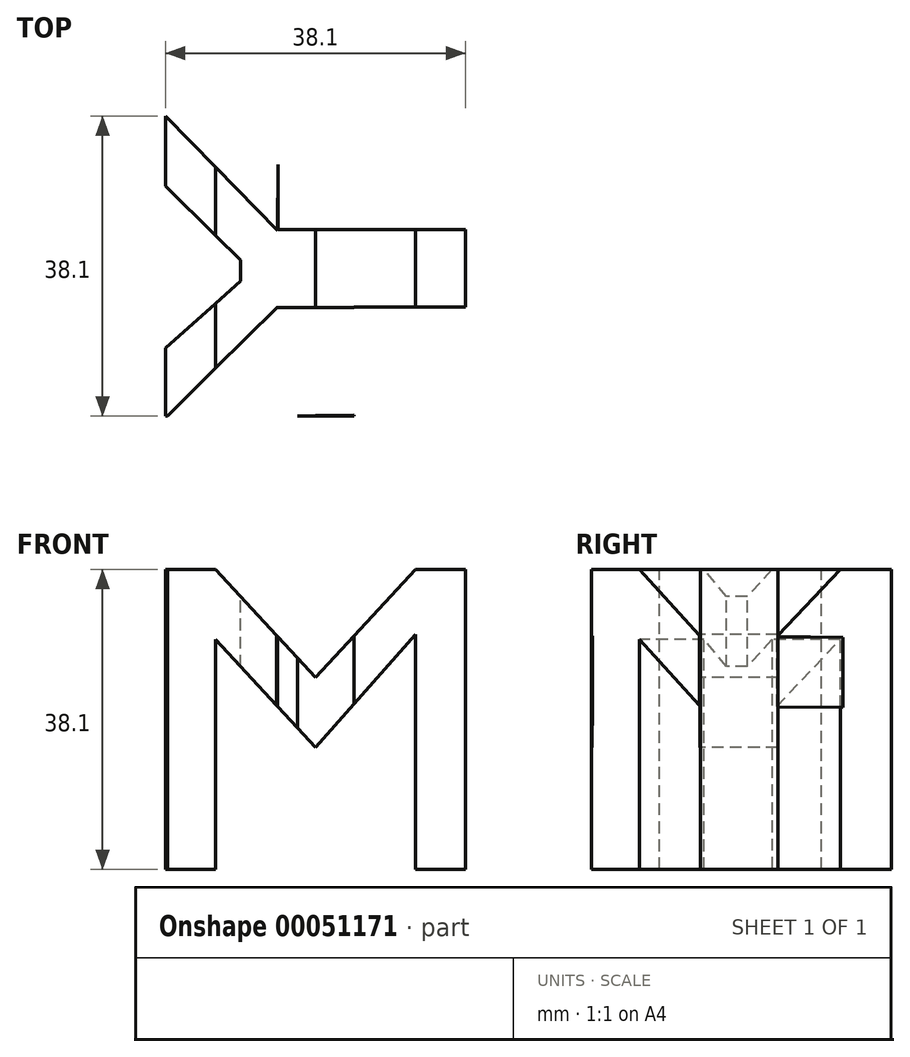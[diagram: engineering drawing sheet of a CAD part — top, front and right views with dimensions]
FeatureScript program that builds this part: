
annotation { "Feature Type Name" : "Feature", "Feature Type Description" : "" }
export const myFeature = defineFeature(function(context is Context, id is Id, definition is map)
    precondition{}
    {
        {
            var Q0;
            Q0=qCreatedBy(makeId("Front.planeOp"),FACE);
            var sketch = newSketch(context, id + "F0", { "sketchPlane" : qUnion([Q0])});
            skLineSegment(sketch, "E0.bottom", {"start": v(0, 0) * mm, "end": v(38.1, 0) * mm});
            skLineSegment(sketch, "E0.top", {"start": v(0, 38.1) * mm, "end": v(38.1, 38.1) * mm});
            skLineSegment(sketch, "E0.left", {"start": v(0, 0) * mm, "end": v(0, 38.1) * mm});
            skLineSegment(sketch, "E0.right", {"start": v(38.1, 0) * mm, "end": v(38.1, 38.1) * mm});
            skSolve(sketch);
        }
        {
            var Q0;
            Q0 = qSketchRegion(id + "F0", true);
            extrude(context, id + "F1", {"entities" : qUnion([Q0]), "depth" : 38.1 * mm});
        }
        {
            var Q0;
            Q0=makeQuery(id+"F1.opExtrude","CAP_FACE",FACE,{"disambiguationData":[OSD([sQuery(id+"F0.wireOp",EDGE,"E0.bottom"),sQuery(id+"F0.wireOp",EDGE,"E0.top"),sQuery(id+"F0.wireOp",EDGE,"E0.left"),sQuery(id+"F0.wireOp",EDGE,"E0.right")])],"isStart":false});
            var sketch = newSketch(context, id + "F2", { "sketchPlane" : qUnion([Q0])});
            skLineSegment(sketch, "E1", {"start": v(0, 38.1) * mm, "end": v(6.35, 38.1) * mm});
            skLineSegment(sketch, "E2", {"start": v(31.75, 38.1) * mm, "end": v(38.1, 38.1) * mm});
            skLineSegment(sketch, "E3", {"start": v(6.35, 38.1) * mm, "end": v(19.02, 24.39) * mm});
            skLineSegment(sketch, "E4", {"start": v(19.02, 24.39) * mm, "end": v(31.75, 38.1) * mm});
            skLineSegment(sketch, "E5", {"start": v(6.35, 29.21) * mm, "end": v(19.02, 15.5) * mm});
            skLineSegment(sketch, "E6", {"start": v(19.02, 15.5) * mm, "end": v(31.75, 29.87) * mm});
            skLineSegment(sketch, "E7", {"start": v(6.35, 29.21) * mm, "end": v(6.35, 0) * mm});
            skLineSegment(sketch, "E8", {"start": v(6.35, 29.21) * mm, "end": v(6.35, 38.1) * mm});
            skLineSegment(sketch, "E9", {"start": v(31.75, 38.1) * mm, "end": v(31.75, 0) * mm});
            skLineSegment(sketch, "E10", {"start": v(6.35, 0) * mm, "end": v(31.75, 0) * mm});
            skLineSegment(sketch, "E11", {"start": v(31.75, 29.87) * mm, "end": v(31.75, 0) * mm});
            skSolve(sketch);
        }
        {
            var Q0;
            {var subQ0=sQuery(id+"F2.wireOp",EDGE,"E3");Q0=makeQuery(id+"F2.imprint","IMPRINT",FACE,{"disambiguationData":[TD([[makeQuery(id+"F2.imprint","IMPRINT",EDGE,{"derivedFrom":subQ0}),1.0]])]});}
            extrude(context, id + "F3", {"entities" : qUnion([Q0]), "operationType" : NewBodyOperationType.REMOVE, "oppositeDirection" : true, "depth" : 38.1 * mm});
        }
        {
            var Q0;
            Q0=makeQuery(id+"F2.imprint","IMPRINT",FACE,{"disambiguationData":[TD([[makeQuery(id+"F2.imprint","IMPRINT",EDGE,{"derivedFrom":sQuery(id+"F2.wireOp",EDGE,"E5")}),-1.0]])]});
            extrude(context, id + "F4", {"entities" : qUnion([Q0]), "operationType" : NewBodyOperationType.REMOVE, "oppositeDirection" : true, "depth" : 38.1 * mm});
        }
        {
            var Q0;
            Q0=qCreatedBy(makeId("Top.planeOp"),FACE);
            cPlane(context, id + "F5", {"entities" : qUnion([Q0]), "cplaneType" : CPlaneType.OFFSET, "offset" : 38.1 * mm, "width" : 152.4 * mm, "height" : 152.4 * mm});
        }
        {
            var Q0;
            Q0=qCreatedBy(id+"F5.planeOp",FACE);
            var sketch = newSketch(context, id + "F6", { "sketchPlane" : qUnion([Q0])});
            skLineSegment(sketch, "E12", {"start": v(0, -38.33) * mm, "end": v(14.2, -24.26) * mm});
            skLineSegment(sketch, "E13", {"start": v(0, 0) * mm, "end": v(14.2, -14.53) * mm});
            skLineSegment(sketch, "E14", {"start": v(14.2, -14.53) * mm, "end": v(14.2, -24.26) * mm});
            skLineSegment(sketch, "E15", {"start": v(0, -29.44) * mm, "end": v(9.54, -20.94) * mm});
            skLineSegment(sketch, "E16", {"start": v(9.54, -20.94) * mm, "end": v(9.54, -18.3) * mm});
            skLineSegment(sketch, "E17", {"start": v(9.54, -18.3) * mm, "end": v(0, -8.9) * mm});
            skLineSegment(sketch, "E18", {"start": v(0, -8.9) * mm, "end": v(0, 0) * mm});
            skLineSegment(sketch, "E19", {"start": v(0, -38.33) * mm, "end": v(0, -29.44) * mm});
            skLineSegment(sketch, "E20", {"start": v(0, -29.44) * mm, "end": v(0, -8.9) * mm});
            skLineSegment(sketch, "E21", {"start": v(0, -38.33) * mm, "end": v(14.1, -38.33) * mm});
            skLineSegment(sketch, "E22", {"start": v(14.1, -38.33) * mm, "end": v(14.2, -24.26) * mm});
            skLineSegment(sketch, "E23", {"start": v(14.4, 0) * mm, "end": v(14.2, -14.53) * mm});
            skLineSegment(sketch, "E24", {"start": v(0, 0) * mm, "end": v(14.4, 0) * mm});
            skLineSegment(sketch, "E25", {"start": v(38.2, -38.13) * mm, "end": v(23.92, -38.13) * mm});
            skLineSegment(sketch, "E26", {"start": v(23.92, -38.13) * mm, "end": v(23.92, -24.26) * mm});
            skLineSegment(sketch, "E27", {"start": v(23.92, -24.26) * mm, "end": v(38.2, -24.26) * mm});
            skLineSegment(sketch, "E28", {"start": v(38.2, -24.26) * mm, "end": v(38.2, -38.13) * mm});
            skLineSegment(sketch, "E29", {"start": v(23.92, -14.42) * mm, "end": v(38.2, -14.42) * mm});
            skLineSegment(sketch, "E30", {"start": v(38.2, -14.42) * mm, "end": v(38.2, 0) * mm});
            skLineSegment(sketch, "E31", {"start": v(38.2, 0) * mm, "end": v(24.03, 0) * mm});
            skLineSegment(sketch, "E32", {"start": v(24.03, 0) * mm, "end": v(23.92, -14.42) * mm});
            skLineSegment(sketch, "E33", {"start": v(14.2, -24.26) * mm, "end": v(23.92, -24.26) * mm});
            skLineSegment(sketch, "E34", {"start": v(14.2, -14.53) * mm, "end": v(23.92, -14.42) * mm});
            skLineSegment(sketch, "E35", {"start": v(14.4, 0) * mm, "end": v(0, 0) * mm});
            skLineSegment(sketch, "E36", {"start": v(24.03, 0) * mm, "end": v(14.4, 0) * mm});
            skLineSegment(sketch, "E37", {"start": v(23.92, -38.13) * mm, "end": v(14.1, -38.33) * mm});
            skLineSegment(sketch, "E38", {"start": v(14.1, -37.28) * mm, "end": v(14.1, -38.33) * mm});
            skSolve(sketch);
        }
        {
            var Q0;
            Q0=makeQuery(id+"F6.imprint","IMPRINT",FACE,{"disambiguationData":[TD([[makeQuery(id+"F6.imprint","IMPRINT",EDGE,{"derivedFrom":sQuery(id+"F6.wireOp",EDGE,"E25")}),-1.0]])]});
            var Q1;
            Q1=makeQuery(id+"F6.imprint","IMPRINT",FACE,{"disambiguationData":[TD([[makeQuery(id+"F6.imprint","IMPRINT",EDGE,{"derivedFrom":sQuery(id+"F6.wireOp",EDGE,"E29")}),1.0]])]});
            var Q2;
            Q2=makeQuery(id+"F6.imprint","IMPRINT",FACE,{"disambiguationData":[TD([[makeQuery(id+"F6.imprint","IMPRINT",EDGE,{"derivedFrom":sQuery(id+"F6.wireOp",EDGE,"E13")}),1.0]])]});
            var Q3;
            Q3=makeQuery(id+"F6.imprint","IMPRINT",FACE,{"disambiguationData":[TD([[makeQuery(id+"F6.imprint","IMPRINT",EDGE,{"derivedFrom":sQuery(id+"F6.wireOp",EDGE,"E15")}),1.0]])]});
            var Q4;
            Q4=makeQuery(id+"F6.imprint","IMPRINT",FACE,{"disambiguationData":[TD([[makeQuery(id+"F6.imprint","IMPRINT",EDGE,{"derivedFrom":sQuery(id+"F6.wireOp",EDGE,"E12")}),-1.0]])]});
            extrude(context, id + "F7", {"entities" : qUnion([Q0, Q1, Q2, Q3, Q4]), "operationType" : NewBodyOperationType.REMOVE, "oppositeDirection" : true, "depth" : 38.1 * mm});
        }
        {
            var Q0;
            Q0=qCreatedBy(makeId("Top.planeOp"),FACE);
            var sketch = newSketch(context, id + "F8", { "sketchPlane" : qUnion([Q0])});
            skLineSegment(sketch, "E39", {"start": v(14.26, -14.39) * mm, "end": v(24.1, -14.39) * mm});
            skLineSegment(sketch, "E40", {"start": v(24.1, -14.39) * mm, "end": v(24.1, 0) * mm});
            skLineSegment(sketch, "E41", {"start": v(24.1, 0) * mm, "end": v(14.35, 0) * mm});
            skLineSegment(sketch, "E42", {"start": v(14.1, -38.15) * mm, "end": v(14.1, -24.3) * mm});
            skLineSegment(sketch, "E43", {"start": v(14.1, -24.3) * mm, "end": v(23.93, -24.3) * mm});
            skLineSegment(sketch, "E44", {"start": v(23.93, -24.3) * mm, "end": v(23.93, -37.97) * mm});
            skLineSegment(sketch, "E45", {"start": v(23.93, -37.97) * mm, "end": v(14.1, -38.15) * mm});
            skLineSegment(sketch, "E46", {"start": v(14.35, 0) * mm, "end": v(14.26, -14.39) * mm});
            skSolve(sketch);
        }
        {
            var Q0;
            Q0 = qSketchRegion(id + "F8", true);
            extrude(context, id + "F9", {"entities" : qUnion([Q0]), "operationType" : NewBodyOperationType.REMOVE, "depth" : 38.1 * mm});
        }
    });
